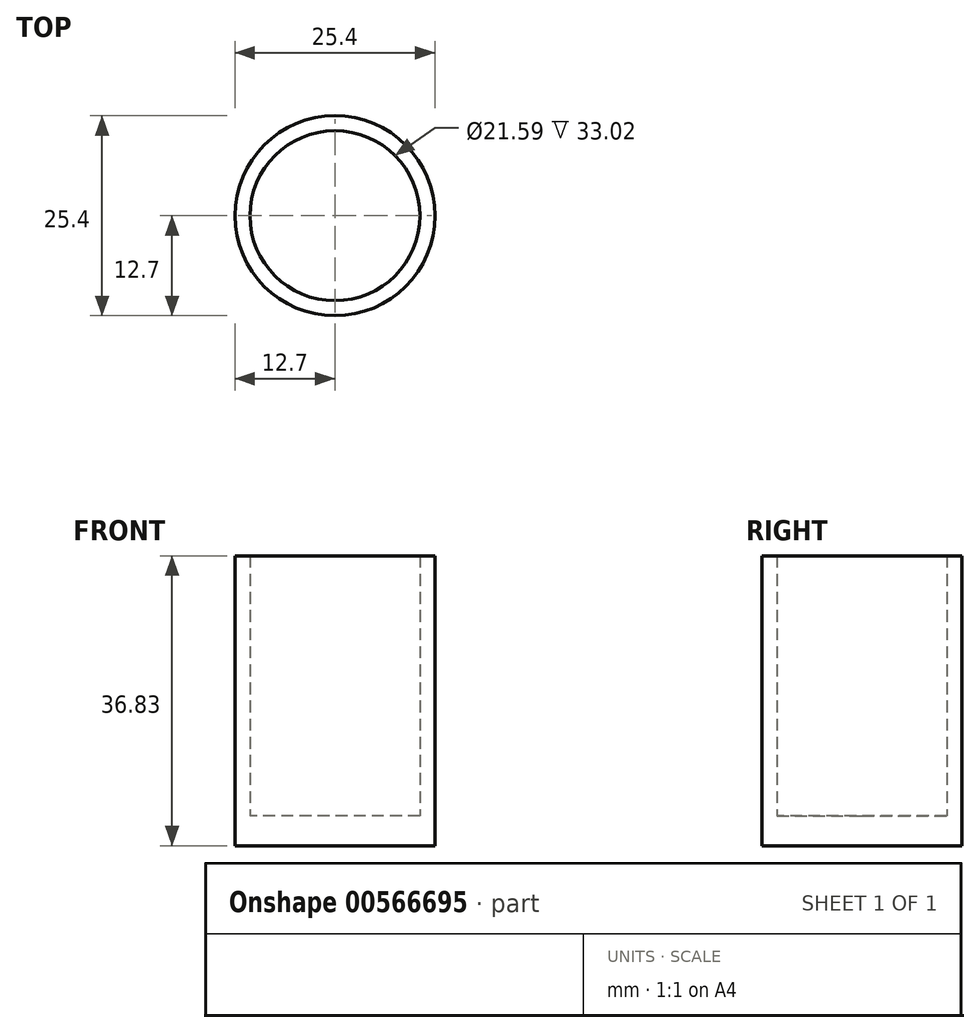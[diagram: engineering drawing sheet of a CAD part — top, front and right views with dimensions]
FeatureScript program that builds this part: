
annotation { "Feature Type Name" : "Feature", "Feature Type Description" : "" }
export const myFeature = defineFeature(function(context is Context, id is Id, definition is map)
    precondition{}
    {
        {
            var Q0;
            Q0=qCreatedBy(makeId("Top.planeOp"),FACE);
            var sketch = newSketch(context, id + "F0", { "sketchPlane" : qUnion([Q0])});
            skCircle(sketch, "E0", {"center": v(0, 0) * mm, "radius": 12.7 * mm});
            skCircle(sketch, "E1", {"center": v(0, 0) * mm, "radius": 10.8 * mm});
            skSolve(sketch);
        }
        {
            var Q0;
            Q0=makeQuery(id+"F0.imprint","IMPRINT",FACE,{"disambiguationData":[TD([[makeQuery(id+"F0.imprint","IMPRINT",EDGE,{"derivedFrom":sQuery(id+"F0.wireOp",EDGE,"E0")}),1.0]])]});
            extrude(context, id + "F1", {"entities" : qUnion([Q0]), "depth" : 33.02 * mm, "offsetDistance" : 25.4 * mm});
        }
        {
            var Q0;
            Q0=makeQuery(id+"F1.opExtrude","CAP_FACE",FACE,{"disambiguationData":[OSD([sQuery(id+"F0.wireOp",EDGE,"E0"),sQuery(id+"F0.wireOp",EDGE,"E1")])],"isStart":true});
            var sketch = newSketch(context, id + "F2", { "sketchPlane" : qUnion([Q0])});
            skCircle(sketch, "E2.0", {"center": v(0, 0) * mm, "radius": 12.7 * mm});
            skSolve(sketch);
        }
        {
            var Q0;
            Q0=makeQuery(id+"F2.imprint","IMPRINT",FACE,{"disambiguationData":[TD([[makeQuery(id+"F2.imprint","IMPRINT",EDGE,{"derivedFrom":sQuery(id+"F2.wireOp",EDGE,"E2.0")}),-1.0]])]});
            var Q1;
            Q1=makeQuery(id+"F2.imprint","IMPRINT",FACE,{"disambiguationData":[TD([[makeQuery(id+"F2.imprint","IMPRINT",EDGE,{"derivedFrom":makeQuery(id+"F1.opExtrude","CAP_EDGE",EDGE,{"disambiguationData":[OSD([sQuery(id+"F0.wireOp",EDGE,"E1")])],"isStart":true})}),-1.0]])]});
            extrude(context, id + "F3", {"entities" : qUnion([Q0, Q1]), "operationType" : NewBodyOperationType.ADD, "depth" : 3.8 * mm, "offsetDistance" : 25.4 * mm});
        }
    });
